# Revit family: QF_MACOM_CF72C-2M
name_source: partatom
category: Equipamento especial
units: mm (PartAtom-declared; Revit-internal decimal feet)

## family parameters
Com base no plano de trabalho = Não
Compartilhado = Não
Corte com vazios quando carregada = Não
Cota do conector redondo = Utilizar diâmetro
Número OmniClass = 23.40.40.14.17.11
Ponto de cálculo do ambiente = Não
Sempre na vertical = Sim
Tipo de parte = Normal
Título OmniClass = Cookers, Ovens, Stoves

## types (1)
- CF72C-2M
    Capacity = GN 1/1 - 150
    Cycle = 60 Hz
    Depth = 745,00 mm
    Descrição = CONSERVADOR DE FRITURAS 700HP MACOM 720 ELETRICO
    Elec Connection Height = 20,00 mm
    Electric Power = 1380 W
    Elevação padrão = 0,00 mm
    Fabricante = MACOM
    Height = 764,00 mm
    Ingress Protection Code = IP 20
    Modelo = CF72C-2M
    Operational Current = 6 A
    Show Logo = Sim
    URL = https://www.acosmacom.com.br
    Volts = 220 V
    Volume = 0,41 m³
    Weight = 20,00 kg
    Width = 720,00 mm

## geometry (parser evidence)
native form markers: Sweep x5
no freeform markers — native parametric forms only
